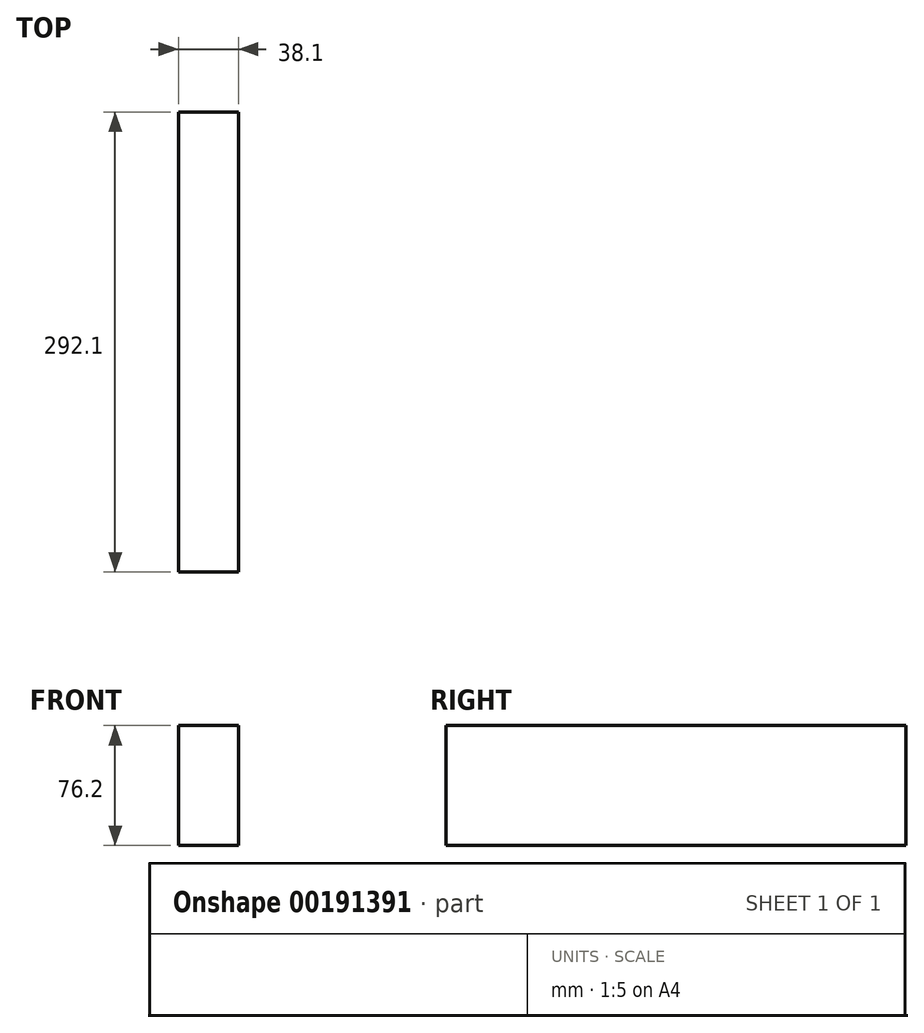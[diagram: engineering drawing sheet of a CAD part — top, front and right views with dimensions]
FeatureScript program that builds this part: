
annotation { "Feature Type Name" : "Feature", "Feature Type Description" : "" }
export const myFeature = defineFeature(function(context is Context, id is Id, definition is map)
    precondition{}
    {
        {
            var Q0;
            Q0=qCreatedBy(makeId("Front.planeOp"),FACE);
            var sketch = newSketch(context, id + "F0", { "sketchPlane" : qUnion([Q0])});
            skLineSegment(sketch, "E0.bottom", {"start": v(-19.05, 38.1) * mm, "end": v(19.05, 38.1) * mm});
            skLineSegment(sketch, "E0.top", {"start": v(-19.05, -38.1) * mm, "end": v(19.05, -38.1) * mm});
            skLineSegment(sketch, "E0.left", {"start": v(-19.05, 38.1) * mm, "end": v(-19.05, -38.1) * mm});
            skLineSegment(sketch, "E0.right", {"start": v(19.05, 38.1) * mm, "end": v(19.05, -38.1) * mm});
            skLineSegment(sketch, "E1", {"start": v(19.05, 38.1) * mm, "end": v(-19.05, -38.1) * mm, "construction": true});
            skSolve(sketch);
        }
        {
            var Q0;
            Q0=makeQuery(id+"F0.imprint","IMPRINT",FACE,{"disambiguationData":[TD([[makeQuery(id+"F0.imprint","IMPRINT",EDGE,{"derivedFrom":sQuery(id+"F0.wireOp",EDGE,"E0.bottom")}),-1.0]])]});
            extrude(context, id + "F1", {"entities" : qUnion([Q0]), "depth" : 292.1 * mm});
        }
    });
